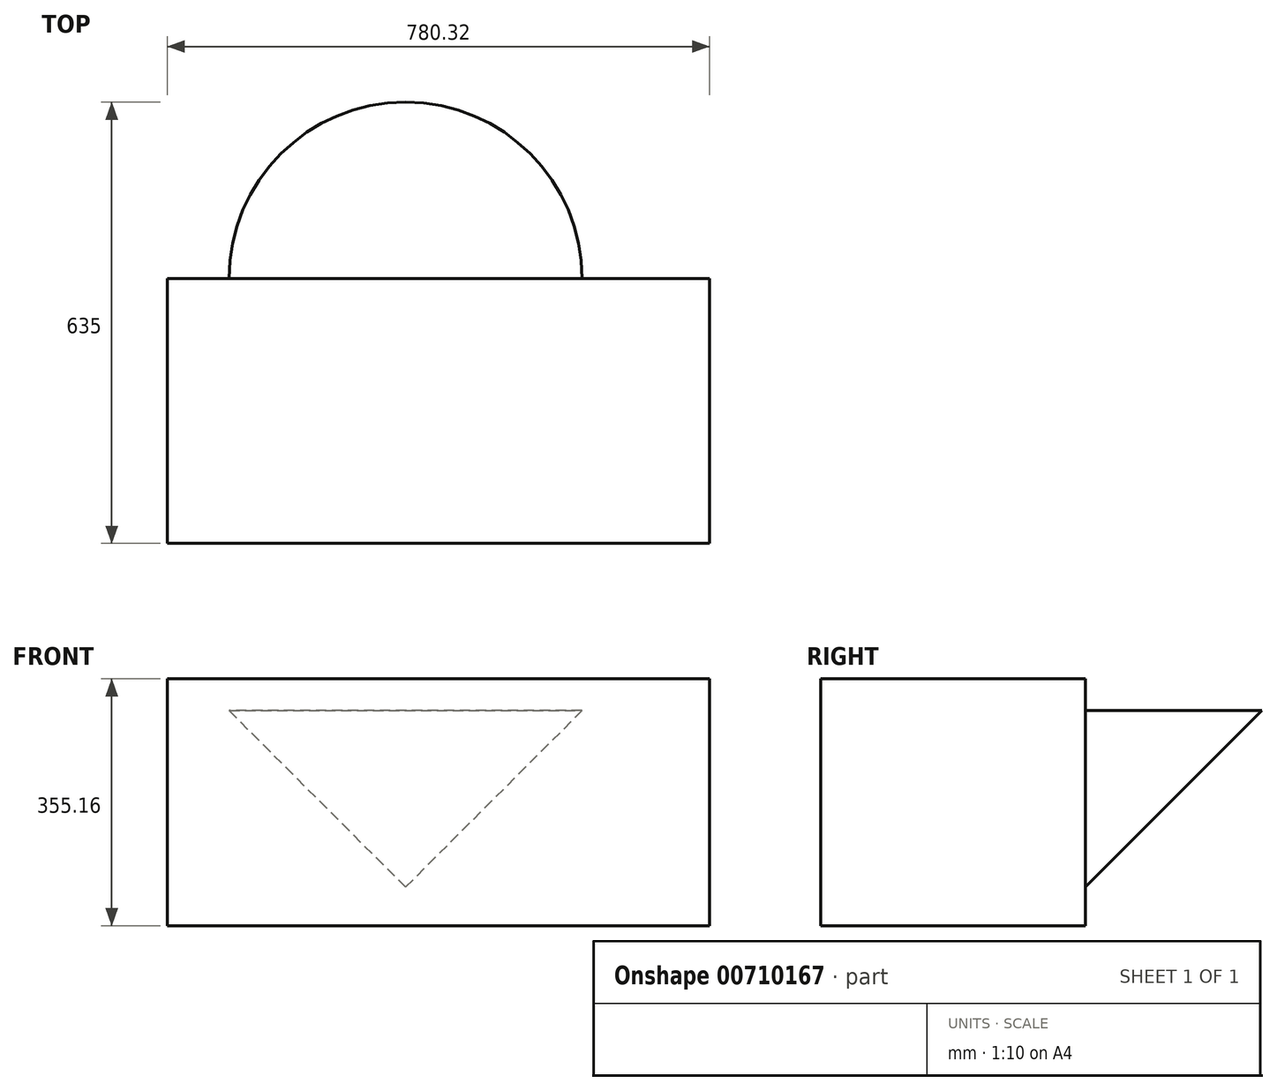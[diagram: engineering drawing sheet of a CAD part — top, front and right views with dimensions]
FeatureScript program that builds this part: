
annotation { "Feature Type Name" : "Feature", "Feature Type Description" : "" }
export const myFeature = defineFeature(function(context is Context, id is Id, definition is map)
    precondition{}
    {
        {
            var Q0;
            Q0=qCreatedBy(makeId("Front.planeOp"),FACE);
            var sketch = newSketch(context, id + "F0", { "sketchPlane" : qUnion([Q0])});
            skLineSegment(sketch, "E0.bottom", {"start": v(-80.59, 172.04) * mm, "end": v(173.41, 172.04) * mm});
            skLineSegment(sketch, "E0.left", {"start": v(-80.59, 172.04) * mm, "end": v(-80.59, -81.96) * mm});
            skLineSegment(sketch, "E1", {"start": v(-80.59, -81.96) * mm, "end": v(173.41, 172.04) * mm});
            skSolve(sketch);
        }
        {
            var Q0;
            Q0 = qSketchRegion(id + "F0", true);
            var Q1;
            Q1=sQuery(id+"F0.wireOp",EDGE,"E0.left");
            revolve(context, id + "F1", {"surfaceOperationType" : NewSurfaceOperationType.NEW, "entities" : qUnion([Q0]), "axis" : qUnion([Q1]), "revolveType" : RevolveType.FULL});
        }
        {
            var Q0;
            Q0=qCreatedBy(makeId("Front.planeOp"),FACE);
            var sketch = newSketch(context, id + "F2", { "sketchPlane" : qUnion([Q0])});
            skLineSegment(sketch, "E2.bottom", {"start": v(-423.47, 217.73) * mm, "end": v(356.85, 217.73) * mm});
            skLineSegment(sketch, "E2.top", {"start": v(-423.47, -137.43) * mm, "end": v(356.85, -137.43) * mm});
            skLineSegment(sketch, "E2.left", {"start": v(-423.47, 217.73) * mm, "end": v(-423.47, -137.43) * mm});
            skLineSegment(sketch, "E2.right", {"start": v(356.85, 217.73) * mm, "end": v(356.85, -137.43) * mm});
            skSolve(sketch);
        }
        {
            var Q0;
            Q0 = qSketchRegion(id + "F2", true);
            extrude(context, id + "F3", {"entities" : qUnion([Q0]), "operationType" : NewBodyOperationType.ADD, "depth" : 381 * mm, "offsetDistance" : 25.4 * mm});
        }
    });
